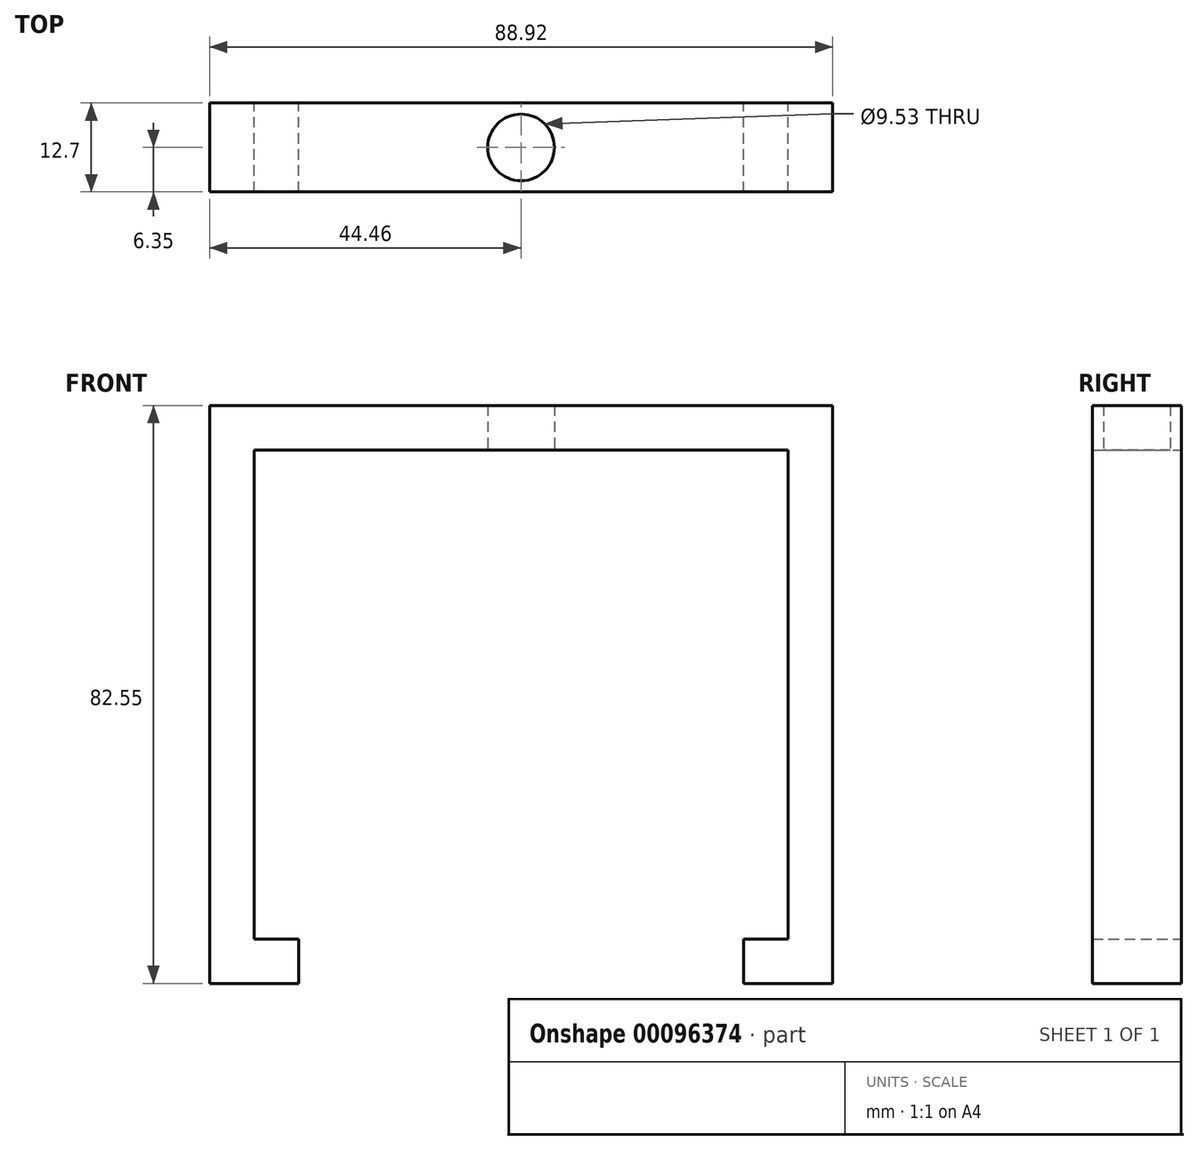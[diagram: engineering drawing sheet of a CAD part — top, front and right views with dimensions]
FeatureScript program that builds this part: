
annotation { "Feature Type Name" : "Feature", "Feature Type Description" : "" }
export const myFeature = defineFeature(function(context is Context, id is Id, definition is map)
    precondition{}
    {
        {
            var Q0;
            Q0=qCreatedBy(makeId("Front.planeOp"),FACE);
            var sketch = newSketch(context, id + "F0", { "sketchPlane" : qUnion([Q0])});
            skPoint(sketch, "E0.middle", {"position": v(0, 0) * mm});
            skPoint(sketch, "E1.endSnap0", {"position": v(0, 57.14) * mm});
            skLineSegment(sketch, "E2.bottom", {"start": v(-38.11, 38.1) * mm, "end": v(38.11, 38.1) * mm});
            skLineSegment(sketch, "E2.left", {"start": v(-38.11, 38.1) * mm, "end": v(-38.11, -38.1) * mm});
            skLineSegment(sketch, "E2.right", {"start": v(38.11, 38.1) * mm, "end": v(38.11, -38.1) * mm});
            skLineSegment(sketch, "E3.bottom", {"start": v(-38.11, -38.1) * mm, "end": v(-31.76, -38.1) * mm});
            skLineSegment(sketch, "E3.top", {"start": v(-38.11, -31.75) * mm, "end": v(-31.76, -31.75) * mm});
            skLineSegment(sketch, "E3.left", {"start": v(-38.11, -38.1) * mm, "end": v(-38.11, -31.75) * mm});
            skLineSegment(sketch, "E3.right", {"start": v(-31.76, -38.1) * mm, "end": v(-31.76, -31.75) * mm});
            skLineSegment(sketch, "E4.MirrorCS", {"start": v(31.76, -38.1) * mm, "end": v(31.76, -31.75) * mm});
            skLineSegment(sketch, "E5.MirrorCS", {"start": v(38.11, -31.75) * mm, "end": v(31.76, -31.75) * mm});
            skLineSegment(sketch, "E6.0", {"start": v(-44.46, 44.45) * mm, "end": v(-44.46, -38.1) * mm});
            skLineSegment(sketch, "E6.1", {"start": v(-44.46, 44.45) * mm, "end": v(44.46, 44.45) * mm});
            skLineSegment(sketch, "E6.2", {"start": v(44.46, 44.45) * mm, "end": v(44.46, -38.1) * mm});
            skLineSegment(sketch, "E7", {"start": v(-44.46, -38.1) * mm, "end": v(-38.11, -38.1) * mm});
            skLineSegment(sketch, "E8", {"start": v(31.76, -38.1) * mm, "end": v(44.46, -38.1) * mm});
            skSolve(sketch);
        }
        {
            var Q0;
            {var subQ2=sQuery(id+"F0.wireOp",EDGE,"E2.left");Q0=makeQuery(id+"F0.imprint","IMPRINT",FACE,{"disambiguationData":[TD([[makeQuery(id+"F0.imprint","IMPRINT",EDGE,{"derivedFrom":subQ2}),-1.0]])]});}
            var Q1;
            Q1=makeQuery(id+"F0.imprint","IMPRINT",FACE,{"disambiguationData":[TD([[makeQuery(id+"F0.imprint","IMPRINT",EDGE,{"derivedFrom":sQuery(id+"F0.wireOp",EDGE,"E3.bottom")}),1.0]])]});
            var Q2;
            {var subQ0=sQuery(id+"F0.wireOp",EDGE,"E6.2");Q2=makeQuery(id+"F0.imprint","IMPRINT",FACE,{"disambiguationData":[TD([[makeQuery(id+"F0.imprint","IMPRINT",EDGE,{"derivedFrom":subQ0}),-1.0]])]});}
            var Q3;
            {var subQ4=sQuery(id+"F0.wireOp",EDGE,"E4.MirrorCS");Q3=makeQuery(id+"F0.imprint","IMPRINT",FACE,{"disambiguationData":[TD([[makeQuery(id+"F0.imprint","IMPRINT",EDGE,{"derivedFrom":subQ4}),-1.0]])]});}
            extrude(context, id + "F1", {"entities" : qUnion([Q0, Q1, Q2, Q3]), "endBound" : BoundingType.SYMMETRIC, "depth" : 12.7 * mm});
        }
        {
            var Q0;
            Q0=qCreatedBy(makeId("Top.planeOp"),FACE);
            var sketch = newSketch(context, id + "F2", { "sketchPlane" : qUnion([Q0])});
            skCircle(sketch, "E9", {"center": v(0, 0) * mm, "radius": 4.76 * mm});
            skSolve(sketch);
        }
        {
            var Q0;
            Q0=makeQuery(id+"F2.imprint","IMPRINT",FACE,{"disambiguationData":[TD([[makeQuery(id+"F2.imprint","IMPRINT",EDGE,{"derivedFrom":sQuery(id+"F2.wireOp",EDGE,"E9")}),1.0]])]});
            extrude(context, id + "F3", {"entities" : qUnion([Q0]), "operationType" : NewBodyOperationType.REMOVE, "depth" : 152.4 * mm});
        }
    });
